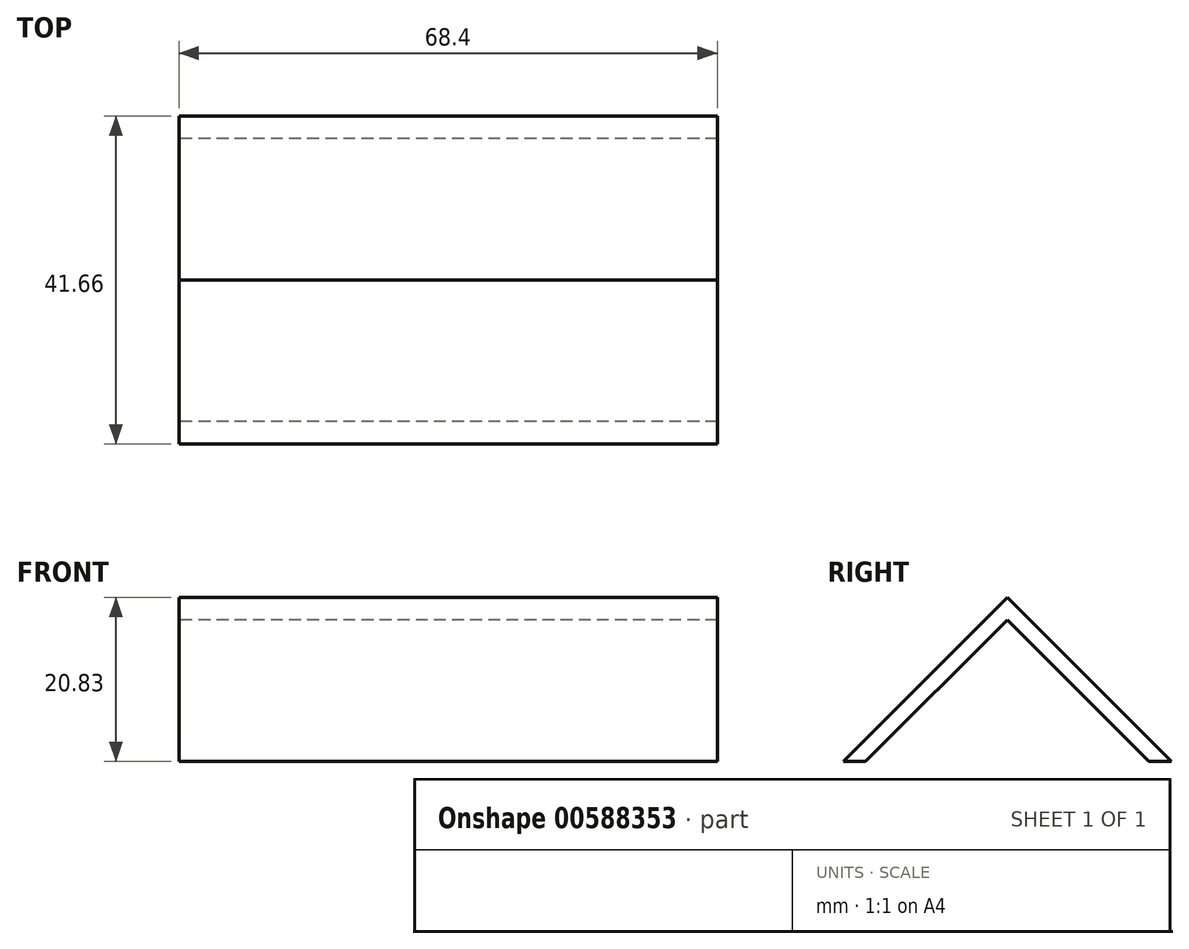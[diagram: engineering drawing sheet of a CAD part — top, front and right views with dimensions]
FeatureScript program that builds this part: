
annotation { "Feature Type Name" : "Feature", "Feature Type Description" : "" }
export const myFeature = defineFeature(function(context is Context, id is Id, definition is map)
    precondition{}
    {
        {
            var Q0;
            Q0=qCreatedBy(makeId("Right.planeOp"),FACE);
            var sketch = newSketch(context, id + "F0", { "sketchPlane" : qUnion([Q0])});
            skLineSegment(sketch, "E0", {"start": v(-106.54, 56.57) * mm, "end": v(-124.54, 38.57) * mm});
            skLineSegment(sketch, "E1", {"start": v(-106.54, 56.57) * mm, "end": v(-88.54, 38.57) * mm});
            skLineSegment(sketch, "E2.0", {"start": v(-106.54, 59.4) * mm, "end": v(-125.96, 39.99) * mm});
            skLineSegment(sketch, "E2.1", {"start": v(-106.54, 59.4) * mm, "end": v(-87.13, 39.99) * mm});
            skLineSegment(sketch, "E3", {"start": v(-88.54, 38.57) * mm, "end": v(-85.71, 38.57) * mm});
            skLineSegment(sketch, "E4", {"start": v(-124.54, 38.57) * mm, "end": v(-127.37, 38.57) * mm});
            skLineSegment(sketch, "E5", {"start": v(-87.13, 39.99) * mm, "end": v(-85.71, 38.57) * mm});
            skLineSegment(sketch, "E6", {"start": v(-125.96, 39.99) * mm, "end": v(-127.37, 38.57) * mm});
            skSolve(sketch);
        }
        {
            var Q0;
            Q0=makeQuery(id+"F0.imprint","IMPRINT",FACE,{"disambiguationData":[TD([[makeQuery(id+"F0.imprint","IMPRINT",EDGE,{"derivedFrom":sQuery(id+"F0.wireOp",EDGE,"E0")}),-1.0]])]});
            extrude(context, id + "F1", {"entities" : qUnion([Q0]), "depth" : 60 * mm, "offsetDistance" : 25 * mm});
        }
        {
            var Q0;
            Q0=makeQuery(id+"F1.opExtrude","CAP_FACE",FACE,{"disambiguationData":[OSD([sQuery(id+"F0.wireOp",EDGE,"E0"),sQuery(id+"F0.wireOp",EDGE,"E1"),sQuery(id+"F0.wireOp",EDGE,"E2.0"),sQuery(id+"F0.wireOp",EDGE,"E2.1"),sQuery(id+"F0.wireOp",EDGE,"E3"),sQuery(id+"F0.wireOp",EDGE,"E4"),sQuery(id+"F0.wireOp",EDGE,"E5"),sQuery(id+"F0.wireOp",EDGE,"E6")])],"isStart":true});
            extrude(context, id + "F2", {"entities" : qUnion([Q0]), "operationType" : NewBodyOperationType.ADD, "depth" : 8.4 * mm, "offsetDistance" : 25 * mm});
        }
    });
